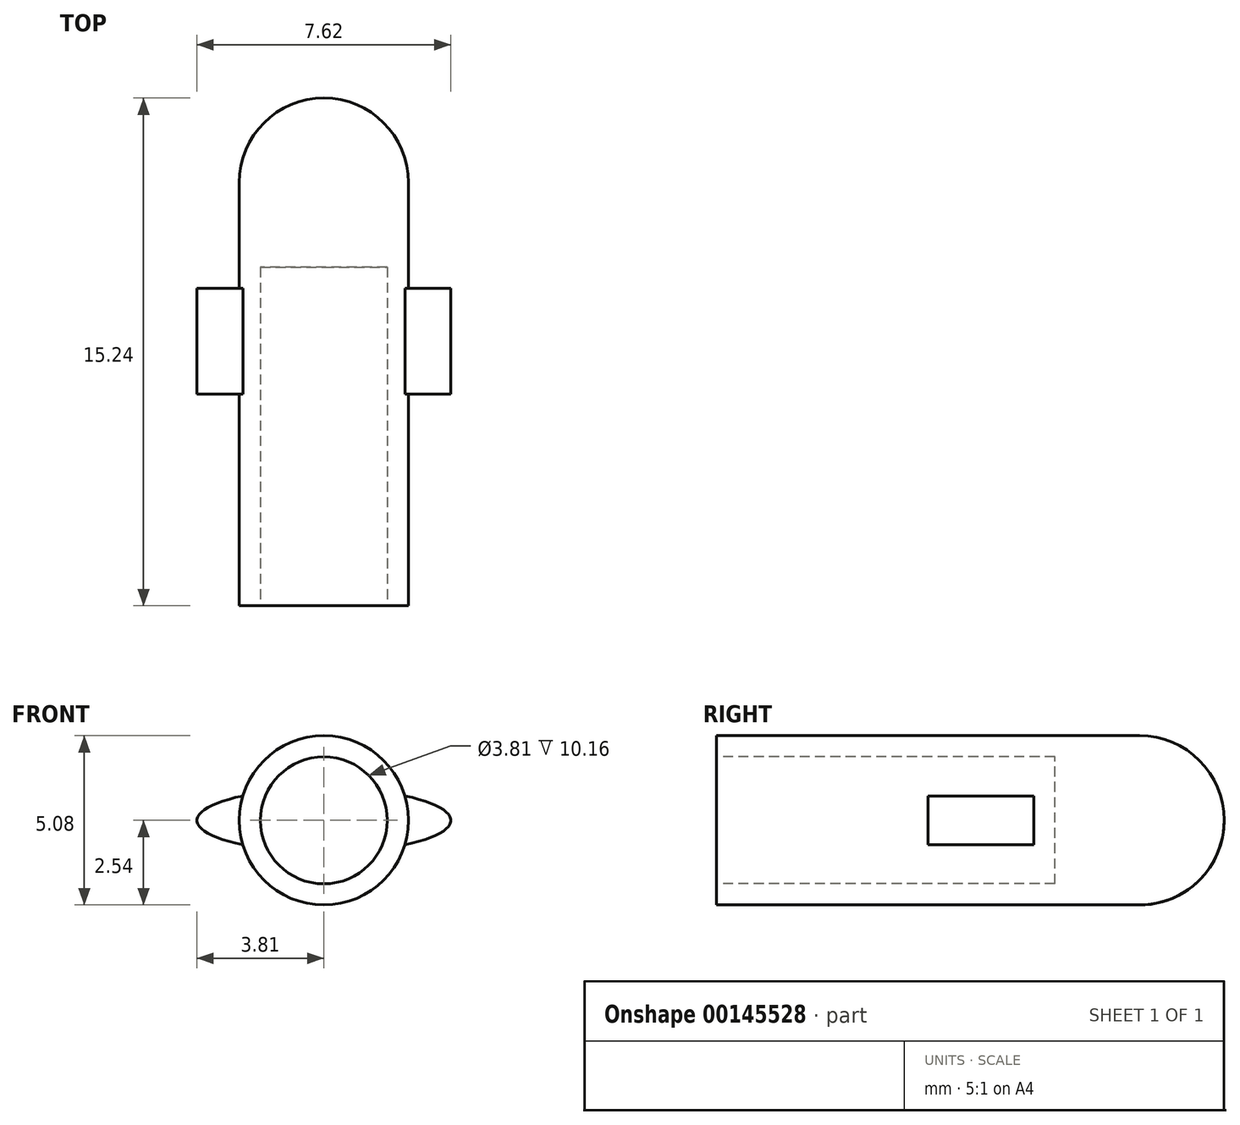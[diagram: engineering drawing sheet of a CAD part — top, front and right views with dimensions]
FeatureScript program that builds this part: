
annotation { "Feature Type Name" : "Feature", "Feature Type Description" : "" }
export const myFeature = defineFeature(function(context is Context, id is Id, definition is map)
    precondition{}
    {
        {
            var Q0;
            Q0=qCreatedBy(makeId("Top.planeOp"),FACE);
            cPlane(context, id + "F0", {"entities" : qUnion([Q0]), "cplaneType" : CPlaneType.OFFSET, "offset" : 2.54 * mm, "width" : 152.4 * mm, "height" : 152.4 * mm});
        }
        {
            var Q0;
            Q0=qCreatedBy(makeId("Front.planeOp"),FACE);
            var sketch = newSketch(context, id + "F1", { "sketchPlane" : qUnion([Q0])});
            skCircle(sketch, "E0", {"center": v(0, 0) * mm, "radius": 2.54 * mm});
            skSolve(sketch);
        }
        {
            var Q0;
            Q0 = qSketchRegion(id + "F1", true);
            extrude(context, id + "F2", {"entities" : qUnion([Q0]), "depth" : 12.7 * mm});
        }
        {
            var Q0;
            Q0=makeQuery(id+"F2.opExtrude","CAP_FACE",FACE,{"disambiguationData":[OSD([sQuery(id+"F1.wireOp",EDGE,"E0")])],"isStart":false});
            var sketch = newSketch(context, id + "F3", { "sketchPlane" : qUnion([Q0])});
            skCircle(sketch, "E1", {"center": v(0, 0) * mm, "radius": 1.9 * mm});
            skSolve(sketch);
        }
        {
            var Q0;
            Q0 = qSketchRegion(id + "F3", true);
            extrude(context, id + "F4", {"entities" : qUnion([Q0]), "operationType" : NewBodyOperationType.REMOVE, "oppositeDirection" : true, "depth" : 10.16 * mm});
        }
        {
            var Q0;
            Q0=qCreatedBy(makeId("Right.planeOp"),FACE);
            var sketch = newSketch(context, id + "F5", { "sketchPlane" : qUnion([Q0])});
            skArc(sketch, "E2", {"start": v(0, 2.54) * mm, "mid": v(1.8, 1.8) * mm, "end": v(2.54, 0) * mm});
            skLineSegment(sketch, "E3", {"start": v(0, 0) * mm, "end": v(2.54, 0) * mm});
            skLineSegment(sketch, "E4", {"start": v(0, 2.54) * mm, "end": v(0, 0) * mm});
            skSolve(sketch);
        }
        {
            var Q0;
            Q0=qCreatedBy(makeId("Right.planeOp"),FACE);
            var sketch = newSketch(context, id + "F6", { "sketchPlane" : qUnion([Q0])});
            skLineSegment(sketch, "E5", {"start": v(1.87, 0) * mm, "end": v(-1.56, 0) * mm, "construction": true});
            skSolve(sketch);
        }
        {
            var Q0;
            Q0 = qSketchRegion(id + "F5", true);
            var Q1;
            Q1=sQuery(id+"F6.wireOp",EDGE,"E5");
            revolve(context, id + "F7", {"operationType" : NewBodyOperationType.ADD, "entities" : qUnion([Q0]), "axis" : qUnion([Q1]), "revolveType" : RevolveType.FULL});
        }
        {
            var Q0;
            Q0=qCreatedBy(makeId("Front.planeOp"),FACE);
            cPlane(context, id + "F8", {"entities" : qUnion([Q0]), "cplaneType" : CPlaneType.OFFSET, "offset" : 3.17 * mm, "width" : 152.4 * mm, "height" : 152.4 * mm});
        }
        {
            var Q0;
            Q0=qCreatedBy(id+"F8.planeOp",FACE);
            var sketch = newSketch(context, id + "F9", { "sketchPlane" : qUnion([Q0])});
            skEllipse(sketch, "E6", {"center": v(0, 0) * mm, "majorRadius": 3.8 * mm, "minorRadius": 0.95 * mm, "majorAxis": v(-1, 0)});
            skSolve(sketch);
        }
        {
            var Q0;
            Q0 = qSketchRegion(id + "F9", true);
            extrude(context, id + "F10", {"entities" : qUnion([Q0]), "operationType" : NewBodyOperationType.ADD, "depth" : 3.17 * mm});
        }
        {
            var Q0;
            {var subQ0=sQuery(id+"F9.wireOp",EDGE,"E6");Q0=makeQuery(id+"F10.boolean.opBoolean","SPLIT",FACE,{"disambiguationData":[TD([makeQuery(id+"F4.boolean.opBoolean","COPY",FACE,{"derivedFrom":makeQuery(id+"F4.opExtrude","SWEPT_FACE",FACE,{"disambiguationData":[OSD([sQuery(id+"F3.wireOp",EDGE,"E1")])]})}),makeQuery(id+"F10.opExtrude","SWEPT_FACE",FACE,{"disambiguationData":[OSD([subQ0])]})])],"derivedFrom":makeQuery(id+"F10.opExtrude","CAP_FACE",FACE,{"disambiguationData":[OSD([subQ0])],"isStart":false})});}
            var sketch = newSketch(context, id + "F11", { "sketchPlane" : qUnion([Q0])});
            skCircle(sketch, "E7", {"center": v(0, 0) * mm, "radius": 1.9 * mm});
            skSolve(sketch);
        }
        {
            var Q0;
            Q0 = qSketchRegion(id + "F11", true);
            extrude(context, id + "F12", {"entities" : qUnion([Q0]), "operationType" : NewBodyOperationType.REMOVE, "oppositeDirection" : true, "depth" : 3.17 * mm});
        }
    });
